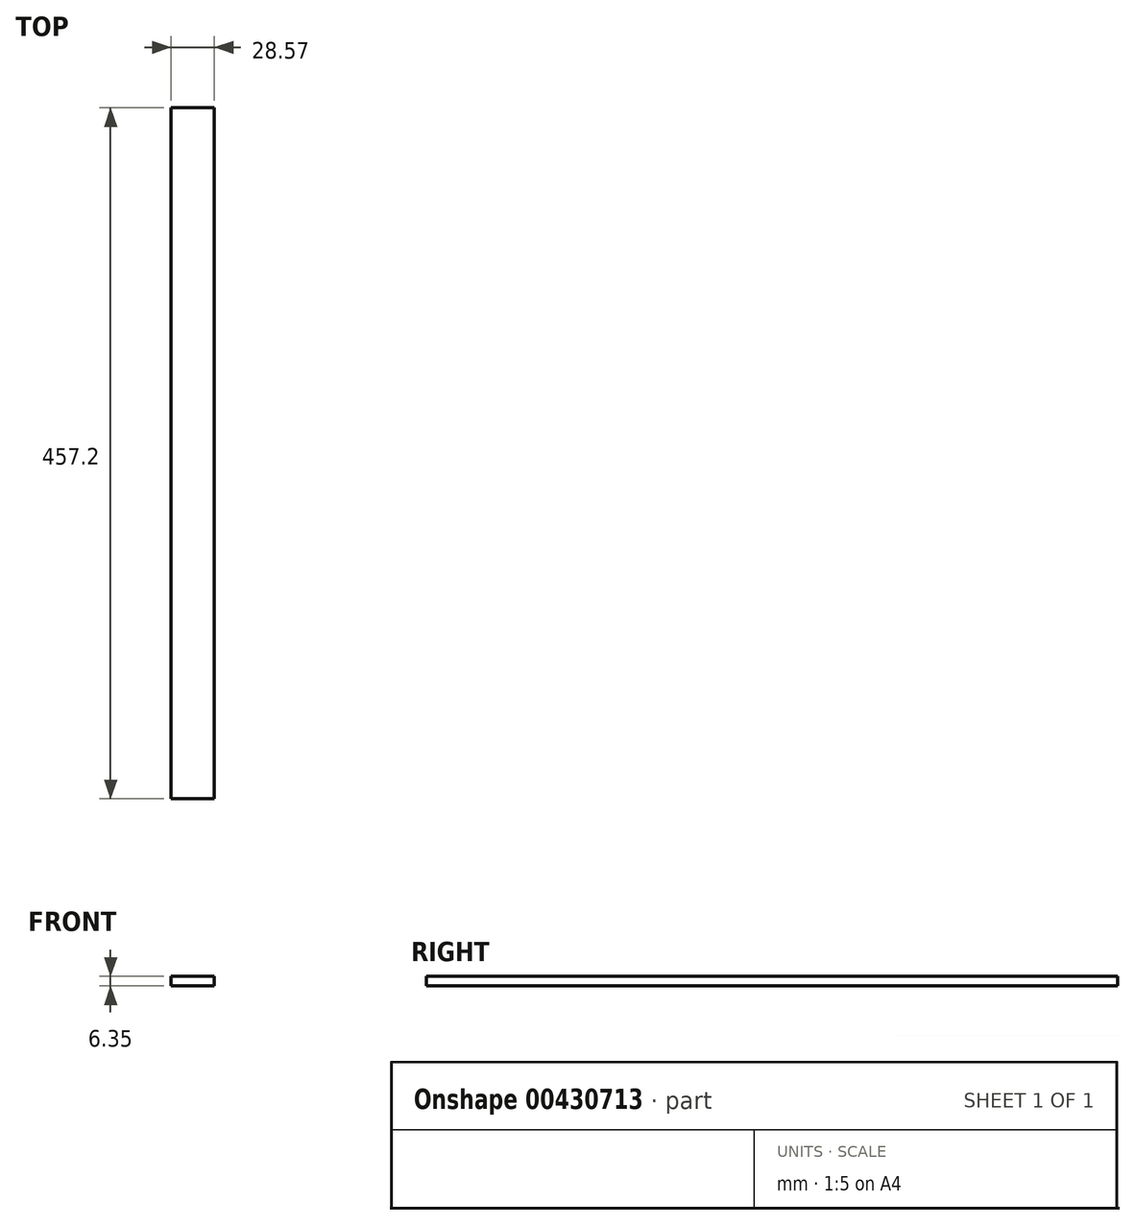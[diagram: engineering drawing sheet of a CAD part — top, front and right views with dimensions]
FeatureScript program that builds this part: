
annotation { "Feature Type Name" : "Feature", "Feature Type Description" : "" }
export const myFeature = defineFeature(function(context is Context, id is Id, definition is map)
    precondition{}
    {
        {
            var Q0;
            Q0=qCreatedBy(makeId("Front.planeOp"),FACE);
            var sketch = newSketch(context, id + "F0", { "sketchPlane" : qUnion([Q0])});
            skLineSegment(sketch, "E0.bottom", {"start": v(0, 0) * mm, "end": v(28.58, 0) * mm});
            skLineSegment(sketch, "E0.top", {"start": v(0, 6.35) * mm, "end": v(28.58, 6.35) * mm});
            skLineSegment(sketch, "E0.left", {"start": v(0, 0) * mm, "end": v(0, 6.35) * mm});
            skLineSegment(sketch, "E0.right", {"start": v(28.58, 0) * mm, "end": v(28.58, 6.35) * mm});
            skSolve(sketch);
        }
        {
            var Q0;
            Q0 = qSketchRegion(id + "F0", true);
            extrude(context, id + "F1", {"entities" : qUnion([Q0]), "depth" : 457.2 * mm, "offsetDistance" : 25.4 * mm});
        }
    });
